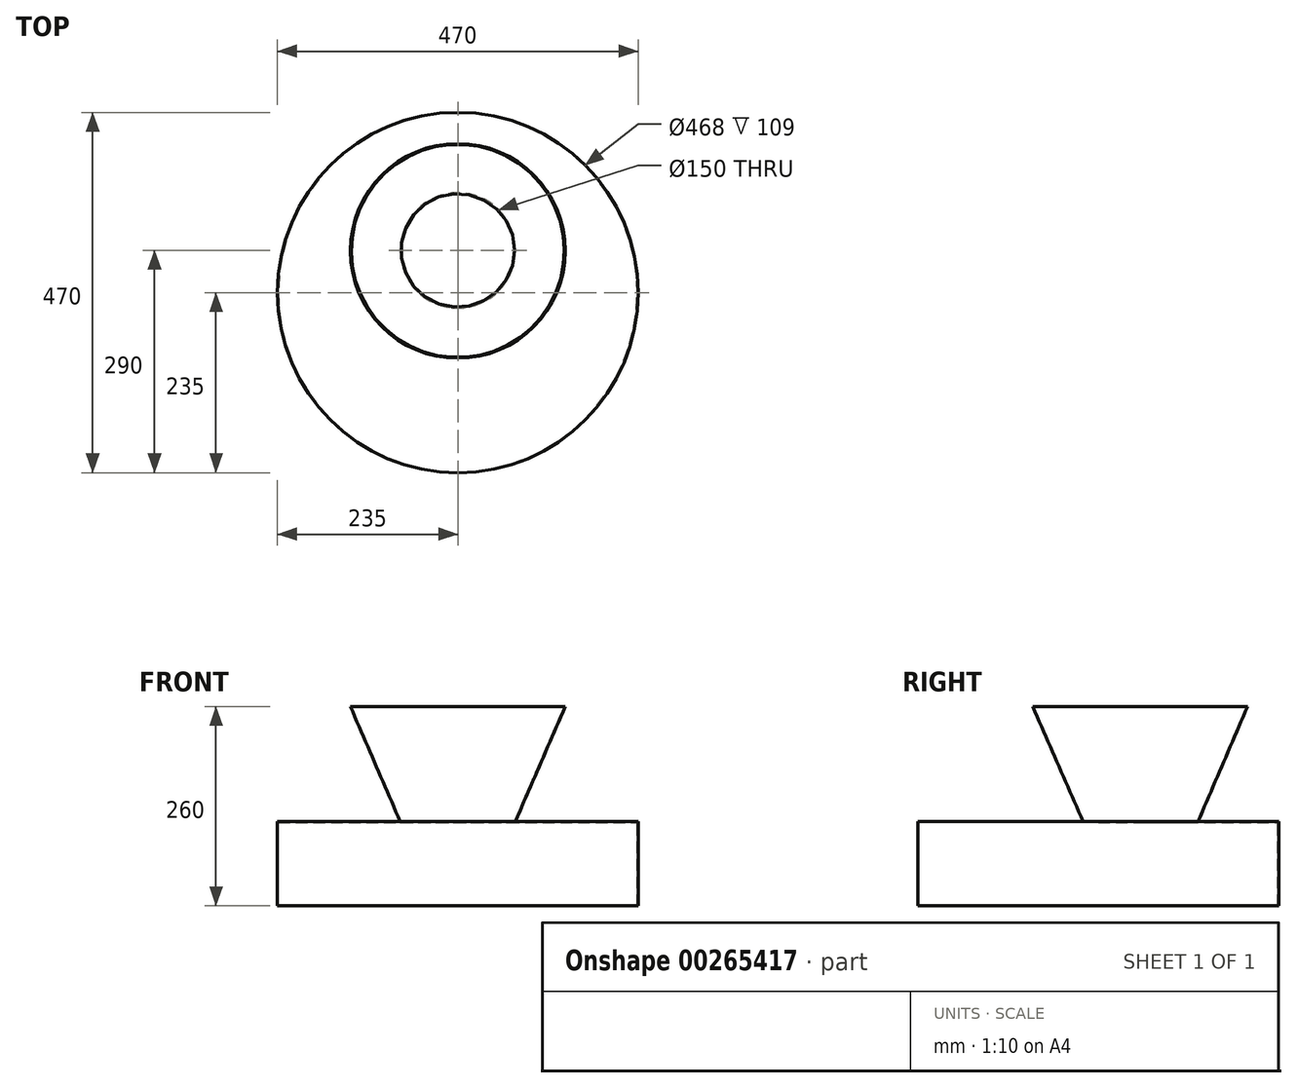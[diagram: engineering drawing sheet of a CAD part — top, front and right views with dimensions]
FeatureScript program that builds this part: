
annotation { "Feature Type Name" : "Feature", "Feature Type Description" : "" }
export const myFeature = defineFeature(function(context is Context, id is Id, definition is map)
    precondition{}
    {
        {
            var Q0;
            Q0=qCreatedBy(makeId("Front.planeOp"),FACE);
            var sketch = newSketch(context, id + "F0", { "sketchPlane" : qUnion([Q0])});
            skLineSegment(sketch, "E0", {"start": v(0, 0) * mm, "end": v(-235, 0) * mm});
            skLineSegment(sketch, "E1", {"start": v(-235, 110) * mm, "end": v(0, 110) * mm});
            skLineSegment(sketch, "E2", {"start": v(-235, 0) * mm, "end": v(-235, 110) * mm});
            skLineSegment(sketch, "E3", {"start": v(0, 110) * mm, "end": v(0, 0) * mm});
            skSolve(sketch);
        }
        {
            var Q0;
            Q0=makeQuery(id+"F0.imprint","IMPRINT",FACE,{"disambiguationData":[TD([[makeQuery(id+"F0.imprint","IMPRINT",EDGE,{"derivedFrom":sQuery(id+"F0.wireOp",EDGE,"E0")}),-1.0]])]});
            var Q1;
            Q1=sQuery(id+"F0.wireOp",EDGE,"E3");
            revolve(context, id + "F1", {"entities" : qUnion([Q0]), "axis" : qUnion([Q1]), "revolveType" : RevolveType.FULL});
        }
        {
            var Q0;
            Q0=makeQuery(id+"F1.opRevolve","SWEPT_FACE",FACE,{"disambiguationData":[OSD([sQuery(id+"F0.wireOp",EDGE,"E0")])]});
            shell(context, id + "F2", {"entities" : qUnion([Q0]), "thickness" : 1 * mm});
        }
        {
            var Q0;
            Q0=makeQuery(id+"F1.opRevolve","SWEPT_FACE",FACE,{"disambiguationData":[OSD([sQuery(id+"F0.wireOp",EDGE,"E1")])]});
            var sketch = newSketch(context, id + "F3", { "sketchPlane" : qUnion([Q0])});
            skLineSegment(sketch, "E4", {"start": v(0, 235) * mm, "end": v(0, 55) * mm});
            skCircle(sketch, "E5", {"center": v(0, 55) * mm, "radius": 140 * mm});
            skCircle(sketch, "E6.0", {"center": v(0, 55) * mm, "radius": 75 * mm});
            skSolve(sketch);
        }
        {
            var Q0;
            Q0=makeQuery(id+"F3.imprint","IMPRINT",FACE,{"disambiguationData":[TD([[makeQuery(id+"F3.imprint","IMPRINT",EDGE,{"derivedFrom":sQuery(id+"F3.wireOp",EDGE,"E5")}),-1.0]])]});
            cPlane(context, id + "F4", {"entities" : qUnion([Q0]), "cplaneType" : CPlaneType.OFFSET, "offset" : 150 * mm, "width" : 150 * mm, "height" : 150 * mm});
        }
        {
            var Q0;
            Q0=qCreatedBy(id+"F4.planeOp",FACE);
            var sketch = newSketch(context, id + "F5", { "sketchPlane" : qUnion([Q0])});
            skCircle(sketch, "E7", {"center": v(0, 54.38) * mm, "radius": 140 * mm});
            skSolve(sketch);
        }
        {
            var Q1;
            Q1=makeQuery(id+"F3.imprint","IMPRINT",FACE,{"disambiguationData":[TD([[makeQuery(id+"F3.imprint","IMPRINT",EDGE,{"derivedFrom":sQuery(id+"F3.wireOp",EDGE,"E6.0")}),1.0]])]});
            var Q2;
            Q2=makeQuery(id+"F5.imprint","IMPRINT",FACE,{"disambiguationData":[TD([[makeQuery(id+"F5.imprint","IMPRINT",EDGE,{"derivedFrom":sQuery(id+"F5.wireOp",EDGE,"E7")}),1.0]])]});
            loft(context, id + "F6", {"operationType" : NewBodyOperationType.ADD, "sheetProfilesArray" : [{ "sheetProfileEntities" : qUnion([Q1]) }, { "sheetProfileEntities" : qUnion([Q2]) }]});
        }
        {
            var Q0;
            Q0=makeQuery(id+"F6.opLoft","CAP_FACE",FACE,{"disambiguationData":[OSD([makeQuery(id+"F5.imprint","IMPRINT",FACE,{"disambiguationData":[TD([[makeQuery(id+"F5.imprint","IMPRINT",EDGE,{"derivedFrom":sQuery(id+"F5.wireOp",EDGE,"E7")}),1.0]])]})])],"isStart":true});
            shell(context, id + "F7", {"entities" : qUnion([Q0]), "thickness" : 1 * mm});
        }
        {
            var Q0;
            Q0=makeQuery(id+"F3.imprint","IMPRINT",FACE,{"disambiguationData":[TD([[makeQuery(id+"F3.imprint","IMPRINT",EDGE,{"derivedFrom":sQuery(id+"F3.wireOp",EDGE,"E6.0")}),1.0]])]});
            extrude(context, id + "F8", {"entities" : qUnion([Q0]), "operationType" : NewBodyOperationType.REMOVE, "oppositeDirection" : true, "depth" : 25 * mm});
        }
    });
